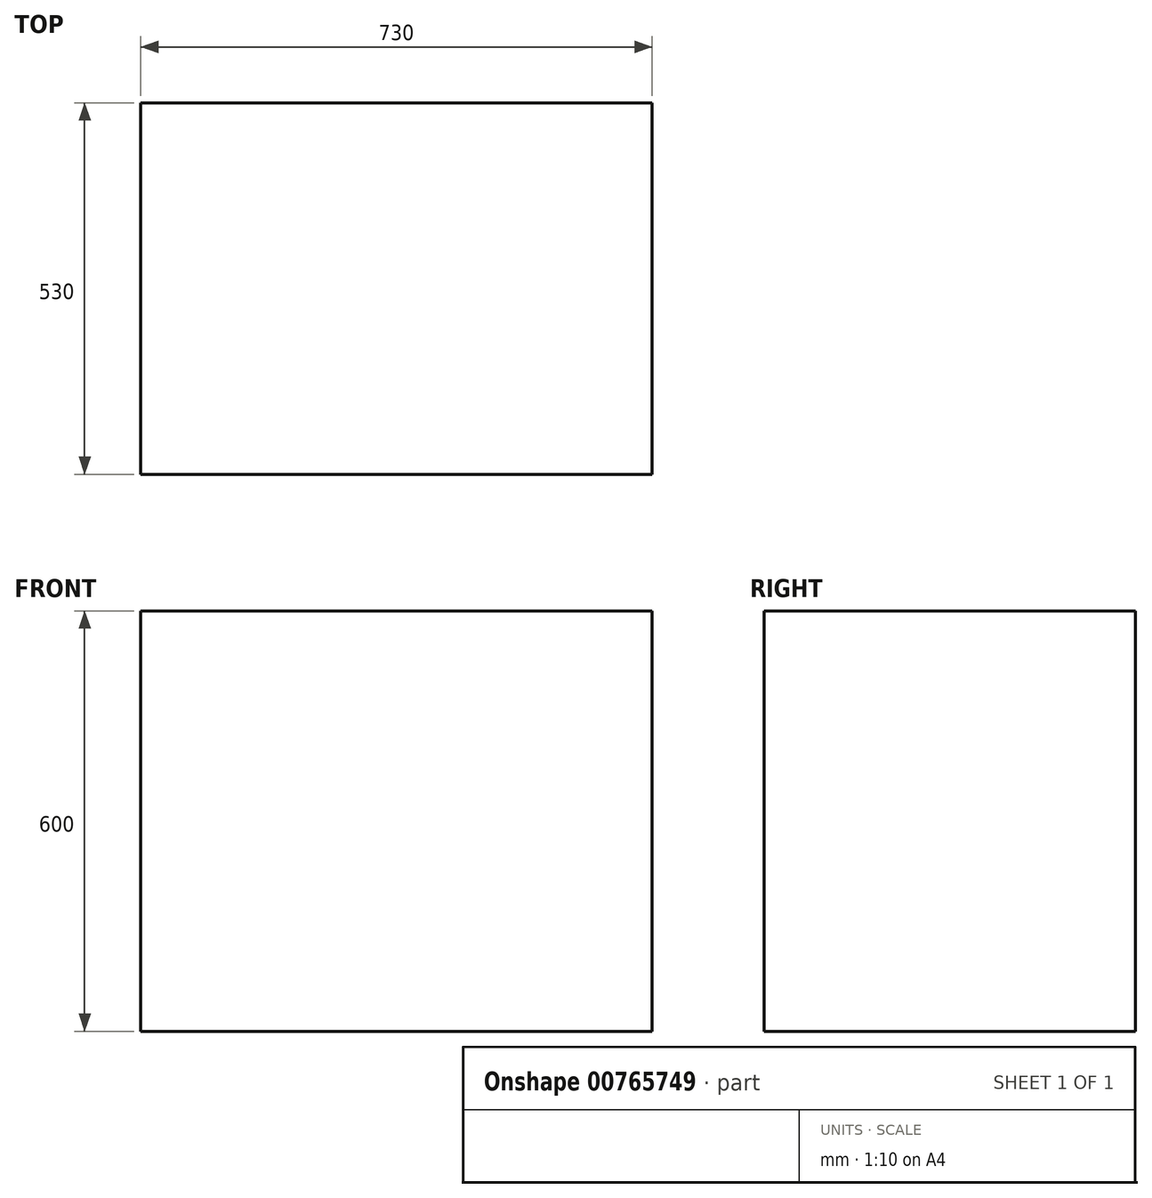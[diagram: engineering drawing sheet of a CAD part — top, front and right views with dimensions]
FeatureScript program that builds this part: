
annotation { "Feature Type Name" : "Feature", "Feature Type Description" : "" }
export const myFeature = defineFeature(function(context is Context, id is Id, definition is map)
    precondition{}
    {
        {
            var Q0;
            Q0=qCreatedBy(makeId("Top.planeOp"),FACE);
            var sketch = newSketch(context, id + "F0", { "sketchPlane" : qUnion([Q0])});
            skLineSegment(sketch, "E0.bottom", {"start": v(365, -265) * mm, "end": v(-365, -265) * mm});
            skLineSegment(sketch, "E0.top", {"start": v(365, 265) * mm, "end": v(-365, 265) * mm});
            skLineSegment(sketch, "E0.left", {"start": v(365, -265) * mm, "end": v(365, 265) * mm});
            skLineSegment(sketch, "E0.right", {"start": v(-365, -265) * mm, "end": v(-365, 265) * mm});
            skPoint(sketch, "E0.middle", {"position": v(0, 0) * mm});
            skSolve(sketch);
        }
        {
            var Q0;
            Q0 = qSketchRegion(id + "F0", true);
            extrude(context, id + "F1", {"entities" : qUnion([Q0]), "depth" : 600 * mm, "offsetDistance" : 25 * mm});
        }
    });
